# Revit family: EBRE-LED-236x-OSx
name_source: partatom
category: Leuchten
units: mm (PartAtom-declared; Revit-internal decimal feet)

## family parameters
Basisbauteil = Fläche
Beim Laden mit Abzugskörper schneiden = Nein
Bemaßung runder Anschluss = Durchmesser verwenden
Gemeinsam genutzt = Nein
Lichtquelle = Ja
OmniClass-Nummer = 23.80.70.11
OmniClass-Titel = Luminaries for Internal Lighting
Raumberechnungspunkt = Nein
Teiletyp = Normal

## types (9) — shared parameters
Baugruppenkennzeichen = D5020200
Datei für fotometrisches Netz = EBRE-LED 2365200840 OS.IES
Emissionsform beim Rendern sichtbar = Nein
Farbfilter = 16777215
Farbtemperaturverschiebung bei Dämpfen der Lampe = <Keine Auswahl>
Hersteller = RIDI Leuchten GmbH
Lampe = LED
Neigungswinkel = 90.00°
URL = www.ridi.de
Von Breite des Rechtecks ausssenden = 1184 mm  [stored 3.88451 ft]
Von Länge des Rechtecks aussenden = 224 mm  [stored 0.734908 ft]
brand = RIDI
conformity mark = CE
electrical safety class = 1
height = 90 mm  [stored 0.295276 ft]
ingress protection (IP) code = IP20
length = 1247 mm  [stored 4.09121 ft]
nominal frequency = 50-60Hz
nominal voltage = 230
voltage type (AC, DC, UC) = AC
weight = 8kg
width = 310 mm  [stored 1.01706 ft]
zero-valued in all types: Vorgabe-Ansicht

## per-type parameters (varying)
| type | Modell | Scheinlast | rated input power |
| EBRE-LED 236/2500-830 OS | 0822855 | 16 VA | 16 |
| EBRE-LED 236/2500-830 OS-DA | 0832855 | 16 VA | 16 |
| EBRE-LED 236/2700-840 OS | 0822839 | 16 VA | 16 |
| EBRE-LED 236/2700-840 OS-DA | 0832839 | 16 VA | 16 |
| EBRE-LED 236/5000-830 OS | 0822851 | 32 VA | 32 |
| EBRE-LED 236/5000-830 OS-DA | 0832851 | 32 VA | 32 |
| EBRE-LED 236/5200-840 OS | 0822816 | 32 VA | 32 |
| EBRE-LED 236/5200-840 OS-DA | 0832816 | 32 VA | 32 |
| EBRE-LED 236/830-865 TW-OS-DA | 0832882 | 32 VA | 32 |

note: column(s) folded — value = type name in every type: product name

note: [stored X ft] marks values corroborated as IEEE doubles in the binary element streams (Revit-internal decimal feet)
